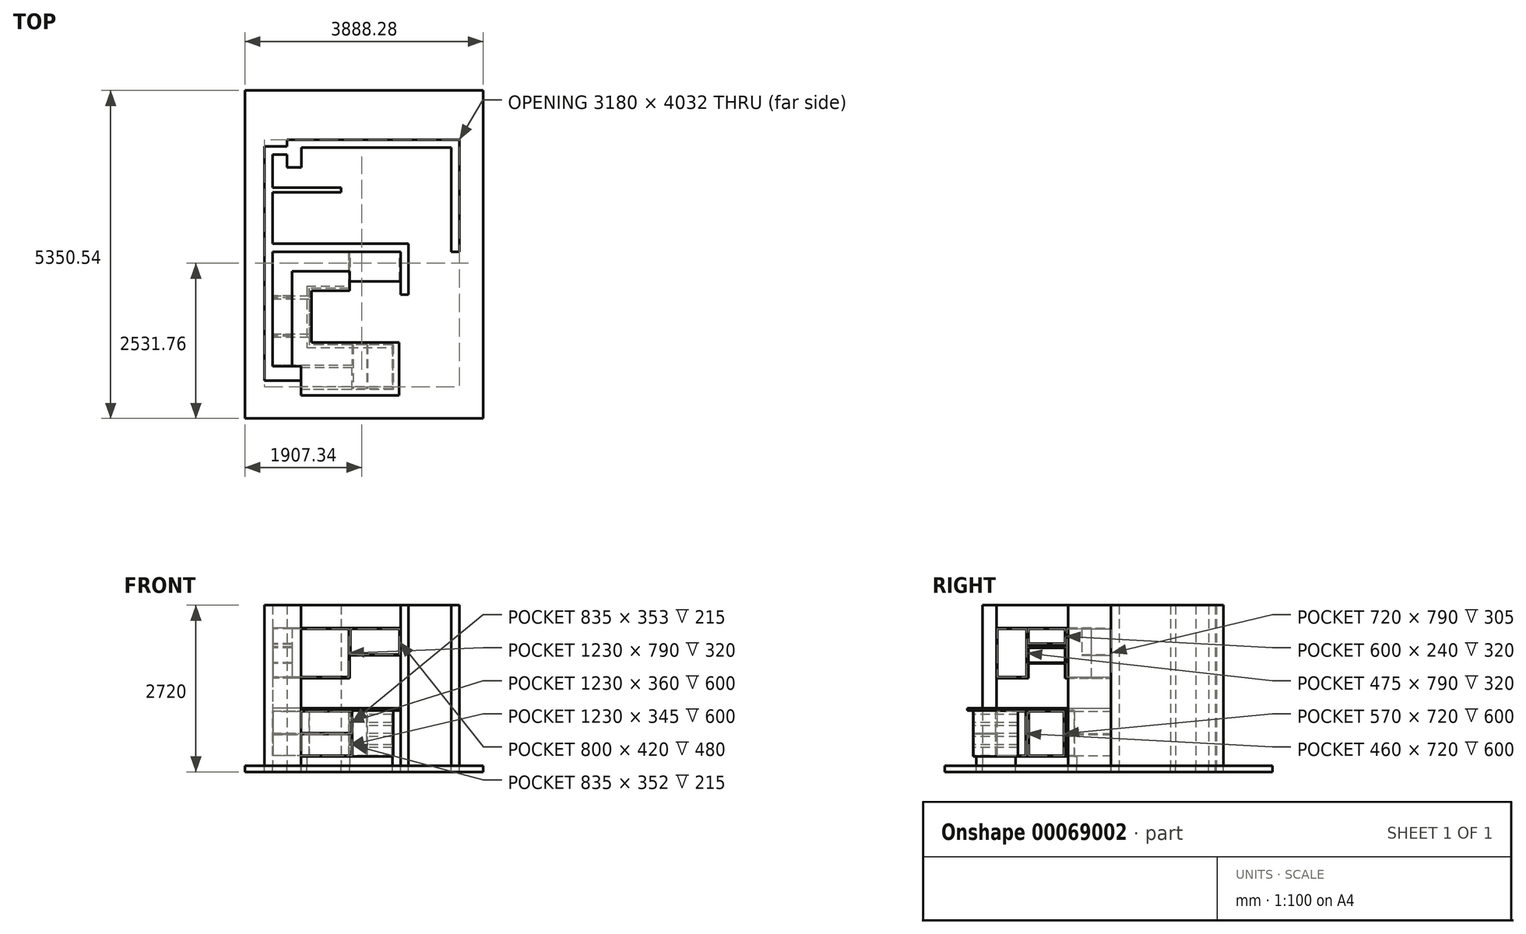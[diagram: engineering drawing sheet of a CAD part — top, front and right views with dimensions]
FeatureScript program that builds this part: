
annotation { "Feature Type Name" : "Feature", "Feature Type Description" : "" }
export const myFeature = defineFeature(function(context is Context, id is Id, definition is map)
    precondition{}
    {
        {
            var Q0;
            Q0=qCreatedBy(makeId("Top.planeOp"),FACE);
            var sketch = newSketch(context, id + "F0", { "sketchPlane" : qUnion([Q0])});
            skLineSegment(sketch, "E0.bottom", {"start": v(-1600, 1700) * mm, "end": v(-1830, 1700) * mm});
            skLineSegment(sketch, "E0.top", {"start": v(-1600, 1250) * mm, "end": v(-1830, 1250) * mm});
            skLineSegment(sketch, "E0.right", {"start": v(-1830, 1700) * mm, "end": v(-1830, 1250) * mm});
            skLineSegment(sketch, "E1", {"start": v(-1830, 1460) * mm, "end": v(-2070, 1460) * mm});
            skLineSegment(sketch, "E2", {"start": v(-1600, 1250) * mm, "end": v(-1600, 1700) * mm});
            skLineSegment(sketch, "E3", {"start": v(-2070, 1460) * mm, "end": v(-2070, -2000) * mm});
            skLineSegment(sketch, "E4.0", {"start": v(-2200, 1590) * mm, "end": v(-2200, -2000) * mm});
            skLineSegment(sketch, "E4.1", {"start": v(-1830, 1590) * mm, "end": v(-2200, 1590) * mm});
            skLineSegment(sketch, "E5.bottom", {"start": v(-2200, -2000) * mm, "end": v(-1605, -2000) * mm});
            skLineSegment(sketch, "E5.top", {"start": v(-2200, -2230) * mm, "end": v(-1605, -2230) * mm});
            skLineSegment(sketch, "E5.left", {"start": v(-2200, -2000) * mm, "end": v(-2200, -2230) * mm});
            skLineSegment(sketch, "E5.right", {"start": v(-1605, -2000) * mm, "end": v(-1605, -2230) * mm});
            skLineSegment(sketch, "E6", {"start": v(980, 1700) * mm, "end": v(980, -132.1) * mm});
            skLineSegment(sketch, "E7", {"start": v(980, -132.1) * mm, "end": v(850, -130) * mm});
            skLineSegment(sketch, "E8", {"start": v(850, 1570) * mm, "end": v(-1600, 1570) * mm});
            skLineSegment(sketch, "E9", {"start": v(980, 1700) * mm, "end": v(-1600, 1700) * mm});
            skLineSegment(sketch, "E10", {"start": v(850, 1570) * mm, "end": v(850, -130) * mm});
            skLineSegment(sketch, "E11", {"start": v(150, 0) * mm, "end": v(-2070, 0) * mm});
            skLineSegment(sketch, "E12.top", {"start": v(150, -830) * mm, "end": v(20, -830) * mm});
            skLineSegment(sketch, "E12.right", {"start": v(20, -130) * mm, "end": v(20, -830) * mm});
            skLineSegment(sketch, "E13", {"start": v(20, -130) * mm, "end": v(-2070, -130) * mm});
            skLineSegment(sketch, "E14", {"start": v(150, 0) * mm, "end": v(150, -830) * mm});
            skLineSegment(sketch, "E15", {"start": v(-1510, -690) * mm, "end": v(-1510, -1690) * mm});
            skLineSegment(sketch, "E16", {"start": v(-1510, -1690) * mm, "end": v(-110, -1690) * mm});
            skLineSegment(sketch, "E17", {"start": v(-1510, -690) * mm, "end": v(-810, -690) * mm});
            skLineSegment(sketch, "E18", {"start": v(-810, -690) * mm, "end": v(-810, -130) * mm});
            skLineSegment(sketch, "E19", {"start": v(-110, -1690) * mm, "end": v(-110, -2332) * mm});
            skLineSegment(sketch, "E20", {"start": v(-110, -2332) * mm, "end": v(-1605, -2332) * mm});
            skLineSegment(sketch, "E21", {"start": v(-1605, -2332) * mm, "end": v(-1605, -2230) * mm});
            skLineSegment(sketch, "E22", {"start": v(-2070, 920) * mm, "end": v(-950, 920) * mm});
            skLineSegment(sketch, "E23", {"start": v(-950, 920) * mm, "end": v(-950, 840) * mm});
            skLineSegment(sketch, "E24", {"start": v(-950, 840) * mm, "end": v(-2070, 840) * mm});
            skSolve(sketch);
        }
        {
            var Q0;
            {var subQ0=sQuery(id+"F0.wireOp",EDGE,"E11");Q0=makeQuery(id+"F0.imprint","IMPRINT",FACE,{"disambiguationData":[TD([[makeQuery(id+"F0.imprint","IMPRINT",EDGE,{"derivedFrom":subQ0}),1.0]])]});}
            var Q1;
            {var subQ3=sQuery(id+"F0.wireOp",EDGE,"E1");Q1=makeQuery(id+"F0.imprint","IMPRINT",FACE,{"disambiguationData":[TD([[makeQuery(id+"F0.imprint","IMPRINT",EDGE,{"derivedFrom":subQ3}),-1.0]])]});}
            var Q2;
            Q2=makeQuery(id+"F0.imprint","IMPRINT",FACE,{"disambiguationData":[TD([[makeQuery(id+"F0.imprint","IMPRINT",EDGE,{"derivedFrom":sQuery(id+"F0.wireOp",EDGE,"E6")}),-1.0]])]});
            var Q3;
            {var subQ3=sQuery(id+"F0.wireOp",EDGE,"E0.bottom");Q3=makeQuery(id+"F0.imprint","IMPRINT",FACE,{"disambiguationData":[TD([[makeQuery(id+"F0.imprint","IMPRINT",EDGE,{"derivedFrom":subQ3}),1.0]])]});}
            var Q4;
            Q4=makeQuery(id+"F0.imprint","IMPRINT",FACE,{"disambiguationData":[TD([[makeQuery(id+"F0.imprint","IMPRINT",EDGE,{"derivedFrom":sQuery(id+"F0.wireOp",EDGE,"E5.top")}),1.0]])]});
            var Q5;
            {var subQ0=sQuery(id+"F0.wireOp",EDGE,"E22");Q5=makeQuery(id+"F0.imprint","IMPRINT",FACE,{"disambiguationData":[TD([[makeQuery(id+"F0.imprint","IMPRINT",EDGE,{"derivedFrom":subQ0}),-1.0]])]});}
            extrude(context, id + "F1", {"entities" : qUnion([Q0, Q1, Q2, Q3, Q4, Q5]), "depth" : 2620 * mm});
        }
        {
            var Q0;
            Q0=makeQuery(id+"F1.opExtrude","SWEPT_FACE",FACE,{"disambiguationData":[OSD([sQuery(id+"F0.wireOp",EDGE,"E13")])]});
            var sketch = newSketch(context, id + "F2", { "sketchPlane" : qUnion([Q0])});
            skLineSegment(sketch, "E25.bottom", {"start": v(-810, 1430) * mm, "end": v(-2070, 1430) * mm});
            skLineSegment(sketch, "E25.top", {"start": v(-810, 2250) * mm, "end": v(-2070, 2250) * mm});
            skLineSegment(sketch, "E25.left", {"start": v(-810, 1430) * mm, "end": v(-810, 2250) * mm});
            skLineSegment(sketch, "E25.right", {"start": v(-2070, 1430) * mm, "end": v(-2070, 2250) * mm});
            skLineSegment(sketch, "E26.0", {"start": v(-825, 2235) * mm, "end": v(-2055, 2235) * mm});
            skLineSegment(sketch, "E26.1", {"start": v(-825, 1445) * mm, "end": v(-825, 2235) * mm});
            skLineSegment(sketch, "E26.2", {"start": v(-825, 1445) * mm, "end": v(-2055, 1445) * mm});
            skLineSegment(sketch, "E26.3", {"start": v(-2055, 1445) * mm, "end": v(-2055, 2235) * mm});
            skSolve(sketch);
        }
        {
            var Q0;
            Q0=makeQuery(id+"F2.imprint","IMPRINT",FACE,{"disambiguationData":[TD([[makeQuery(id+"F2.imprint","IMPRINT",EDGE,{"derivedFrom":sQuery(id+"F2.wireOp",EDGE,"E25.bottom")}),-1.0]])]});
            extrude(context, id + "F3", {"entities" : qUnion([Q0]), "operationType" : NewBodyOperationType.ADD, "depth" : 320 * mm});
        }
        {
            var Q0;
            {var subQ0=sQuery(id+"F0.wireOp",EDGE,"E3");Q0=makeQuery(id+"F1.opExtrude","SWEPT_FACE",FACE,{"disambiguationData":[OSD([subQ0]),TDD([makeQuery(id+"F0.imprint","IMPRINT",EDGE,{"disambiguationData":[TD([[makeQuery(id+"F0.imprint","INTERSECT",VERTEX,{"derivedFrom":[subQ0,sQuery(id+"F0.wireOp",EDGE,"E5.bottom")]}),1.0]])],"derivedFrom":subQ0})])]});}
            var sketch = newSketch(context, id + "F4", { "sketchPlane" : qUnion([Q0])});
            skLineSegment(sketch, "E27.bottom", {"start": v(-450, 2250) * mm, "end": v(-865, 2250) * mm});
            skLineSegment(sketch, "E27.top", {"start": v(-450, 1430) * mm, "end": v(-865, 1430) * mm});
            skLineSegment(sketch, "E27.right", {"start": v(-865, 2250) * mm, "end": v(-865, 1430) * mm});
            skLineSegment(sketch, "E28.0", {"start": v(-850, 2235) * mm, "end": v(-850, 1445) * mm});
            skLineSegment(sketch, "E29", {"start": v(-645, 1445) * mm, "end": v(-645, 2235) * mm});
            skLineSegment(sketch, "E30.0", {"start": v(-630, 1445) * mm, "end": v(-630, 2235) * mm});
            skLineSegment(sketch, "E31", {"start": v(-450, 2250) * mm, "end": v(-450, 2235) * mm});
            skLineSegment(sketch, "E32", {"start": v(-850, 2235) * mm, "end": v(-450, 2235) * mm});
            skLineSegment(sketch, "E33", {"start": v(-450, 1430) * mm, "end": v(-450, 1445) * mm});
            skLineSegment(sketch, "E34", {"start": v(-850, 1445) * mm, "end": v(-450, 1445) * mm});
            skSolve(sketch);
        }
        {
            var Q0;
            Q0=makeQuery(id+"F4.imprint","IMPRINT",FACE,{"disambiguationData":[TD([[makeQuery(id+"F4.imprint","IMPRINT",EDGE,{"derivedFrom":sQuery(id+"F4.wireOp",EDGE,"E27.bottom")}),1.0]])]});
            extrude(context, id + "F5", {"entities" : qUnion([Q0]), "operationType" : NewBodyOperationType.ADD, "depth" : 320 * mm});
        }
        {
            var Q0;
            {var subQ1=sQuery(id+"F2.wireOp",EDGE,"E26.0");var subQ2=sQuery(id+"F0.wireOp",EDGE,"E3");Q0=makeQuery(id+"F5.boolean.opBoolean","SPLIT",FACE,{"disambiguationData":[TD([makeQuery(id+"F3.opExtrude","SWEPT_FACE",FACE,{"disambiguationData":[OSD([subQ1])]})])],"derivedFrom":makeQuery(id+"F1.opExtrude","SWEPT_FACE",FACE,{"disambiguationData":[OSD([subQ2]),TDD([makeQuery(id+"F0.imprint","IMPRINT",EDGE,{"disambiguationData":[TD([[makeQuery(id+"F0.imprint","INTERSECT",VERTEX,{"derivedFrom":[subQ2,sQuery(id+"F0.wireOp",EDGE,"E5.bottom")]}),1.0]])],"derivedFrom":subQ2})])]})});}
            extrude(context, id + "F6", {"entities" : qUnion([Q0]), "operationType" : NewBodyOperationType.ADD, "depth" : 15 * mm});
        }
        {
            var Q0;
            {var subQ2=sQuery(id+"F0.wireOp",EDGE,"E5.bottom");var subQ3=sQuery(id+"F0.wireOp",EDGE,"E3");Q0=makeQuery(id+"F5.boolean.opBoolean","SPLIT",FACE,{"disambiguationData":[TD([makeQuery(id+"F1.opExtrude","SWEPT_FACE",FACE,{"disambiguationData":[OSD([subQ2])]})])],"derivedFrom":makeQuery(id+"F1.opExtrude","SWEPT_FACE",FACE,{"disambiguationData":[OSD([subQ3]),TDD([makeQuery(id+"F0.imprint","IMPRINT",EDGE,{"disambiguationData":[TD([[makeQuery(id+"F0.imprint","INTERSECT",VERTEX,{"derivedFrom":[subQ3,subQ2]}),1.0]])],"derivedFrom":subQ3})])]})});}
            var sketch = newSketch(context, id + "F7", { "sketchPlane" : qUnion([Q0])});
            skLineSegment(sketch, "E35.bottom", {"start": v(-865, 2250) * mm, "end": v(-1495, 2250) * mm});
            skLineSegment(sketch, "E35.left", {"start": v(-865, 2250) * mm, "end": v(-865, 1430) * mm});
            skLineSegment(sketch, "E35.right", {"start": v(-1495, 2250) * mm, "end": v(-1495, 1430) * mm});
            skLineSegment(sketch, "E36.0", {"start": v(-880, 2235) * mm, "end": v(-880, 1430) * mm});
            skLineSegment(sketch, "E36.1", {"start": v(-880, 2235) * mm, "end": v(-1480, 2235) * mm});
            skLineSegment(sketch, "E36.2", {"start": v(-1480, 2235) * mm, "end": v(-1480, 1430) * mm});
            skLineSegment(sketch, "E37", {"start": v(-1480, 1670) * mm, "end": v(-880, 1670) * mm});
            skLineSegment(sketch, "E38", {"start": v(-1480, 1430) * mm, "end": v(-1495, 1430) * mm});
            skLineSegment(sketch, "E39", {"start": v(-865, 1430) * mm, "end": v(-880, 1430) * mm});
            skLineSegment(sketch, "E40.0", {"start": v(-1480, 1685) * mm, "end": v(-880, 1685) * mm});
            skLineSegment(sketch, "E41", {"start": v(-1480, 1925) * mm, "end": v(-880, 1925) * mm});
            skLineSegment(sketch, "E42", {"start": v(-1480, 1995) * mm, "end": v(-880, 1995) * mm});
            skLineSegment(sketch, "E43.0", {"start": v(-1480, 1980) * mm, "end": v(-880, 1980) * mm});
            skLineSegment(sketch, "E44.0", {"start": v(-1480, 1940) * mm, "end": v(-880, 1940) * mm});
            skSolve(sketch);
        }
        {
            var Q0;
            Q0=makeQuery(id+"F7.imprint","IMPRINT",FACE,{"disambiguationData":[TD([[makeQuery(id+"F7.imprint","IMPRINT",EDGE,{"derivedFrom":sQuery(id+"F7.wireOp",EDGE,"E35.bottom")}),1.0]])]});
            var Q1;
            {var subQ0=sQuery(id+"F7.wireOp",EDGE,"E42");Q1=makeQuery(id+"F7.imprint","IMPRINT",FACE,{"disambiguationData":[TD([[makeQuery(id+"F7.imprint","IMPRINT",EDGE,{"derivedFrom":subQ0}),-1.0]])]});}
            var Q2;
            {var subQ0=sQuery(id+"F7.wireOp",EDGE,"E41");Q2=makeQuery(id+"F7.imprint","IMPRINT",FACE,{"disambiguationData":[TD([[makeQuery(id+"F7.imprint","IMPRINT",EDGE,{"derivedFrom":subQ0}),1.0]])]});}
            var Q3;
            {var subQ0=sQuery(id+"F7.wireOp",EDGE,"E37");Q3=makeQuery(id+"F7.imprint","IMPRINT",FACE,{"disambiguationData":[TD([[makeQuery(id+"F7.imprint","IMPRINT",EDGE,{"derivedFrom":subQ0}),1.0]])]});}
            extrude(context, id + "F8", {"entities" : qUnion([Q0, Q1, Q2, Q3]), "operationType" : NewBodyOperationType.ADD, "depth" : 320 * mm});
        }
        {
            var Q0;
            {var subQ7=sQuery(id+"F0.wireOp",EDGE,"E5.bottom");var subQ8=sQuery(id+"F0.wireOp",EDGE,"E3");var subQ11=makeQuery(id+"F1.opExtrude","SWEPT_FACE",FACE,{"disambiguationData":[OSD([subQ7])]});Q0=makeQuery(id+"F8.boolean.opBoolean","SPLIT",FACE,{"disambiguationData":[TD([subQ11])],"derivedFrom":makeQuery(id+"F5.boolean.opBoolean","SPLIT",FACE,{"disambiguationData":[TD([subQ11])],"derivedFrom":makeQuery(id+"F1.opExtrude","SWEPT_FACE",FACE,{"disambiguationData":[OSD([subQ8]),TDD([makeQuery(id+"F0.imprint","IMPRINT",EDGE,{"disambiguationData":[TD([[makeQuery(id+"F0.imprint","INTERSECT",VERTEX,{"derivedFrom":[subQ8,subQ7]}),1.0]])],"derivedFrom":subQ8})])]})})});}
            var sketch = newSketch(context, id + "F9", { "sketchPlane" : qUnion([Q0])});
            skLineSegment(sketch, "E45.bottom", {"start": v(-1495, 2250) * mm, "end": v(-2000, 2250) * mm});
            skLineSegment(sketch, "E45.top", {"start": v(-1495, 1430) * mm, "end": v(-2000, 1430) * mm});
            skLineSegment(sketch, "E45.left", {"start": v(-1495, 2250) * mm, "end": v(-1495, 1430) * mm});
            skLineSegment(sketch, "E45.right", {"start": v(-2000, 2250) * mm, "end": v(-2000, 1430) * mm});
            skLineSegment(sketch, "E46.0", {"start": v(-1510, 2235) * mm, "end": v(-1985, 2235) * mm});
            skLineSegment(sketch, "E46.1", {"start": v(-1510, 2235) * mm, "end": v(-1510, 1445) * mm});
            skLineSegment(sketch, "E46.2", {"start": v(-1510, 1445) * mm, "end": v(-1985, 1445) * mm});
            skLineSegment(sketch, "E46.3", {"start": v(-1985, 2235) * mm, "end": v(-1985, 1445) * mm});
            skSolve(sketch);
        }
        {
            var Q0;
            Q0=makeQuery(id+"F9.imprint","IMPRINT",FACE,{"disambiguationData":[TD([[makeQuery(id+"F9.imprint","IMPRINT",EDGE,{"derivedFrom":sQuery(id+"F9.wireOp",EDGE,"E45.bottom")}),1.0]])]});
            extrude(context, id + "F10", {"entities" : qUnion([Q0]), "operationType" : NewBodyOperationType.ADD, "depth" : 320 * mm});
        }
        {
            var Q0;
            {var subQ6=sQuery(id+"F0.wireOp",EDGE,"E5.right");Q0=makeQuery(id+"F0.imprint","IMPRINT",FACE,{"disambiguationData":[TD([[makeQuery(id+"F0.imprint","IMPRINT",EDGE,{"derivedFrom":subQ6}),1.0]])]});}
            extrude(context, id + "F11", {"entities" : qUnion([Q0]), "operationType" : NewBodyOperationType.ADD, "depth" : 150 * mm});
        }
        {
            var Q0;
            {var subQ0=sQuery(id+"F0.wireOp",EDGE,"E12.right");var subQ3=sQuery(id+"F0.wireOp",EDGE,"E13");Q0=makeQuery(id+"F3.boolean.opBoolean","SPLIT",FACE,{"disambiguationData":[TD([makeQuery(id+"F1.opExtrude","SWEPT_FACE",FACE,{"disambiguationData":[OSD([subQ0])]})])],"derivedFrom":makeQuery(id+"F1.opExtrude","SWEPT_FACE",FACE,{"disambiguationData":[OSD([subQ3])]})});}
            var sketch = newSketch(context, id + "F12", { "sketchPlane" : qUnion([Q0])});
            skLineSegment(sketch, "E47.bottom", {"start": v(-810, 150) * mm, "end": v(-2070, 150) * mm});
            skLineSegment(sketch, "E47.top", {"start": v(-810, 900) * mm, "end": v(-2070, 900) * mm});
            skLineSegment(sketch, "E47.left", {"start": v(-810, 150) * mm, "end": v(-810, 900) * mm});
            skLineSegment(sketch, "E47.right", {"start": v(-2070, 150) * mm, "end": v(-2070, 900) * mm});
            skLineSegment(sketch, "E48.0", {"start": v(-825, 165) * mm, "end": v(-825, 885) * mm});
            skLineSegment(sketch, "E48.1", {"start": v(-825, 165) * mm, "end": v(-2055, 165) * mm});
            skLineSegment(sketch, "E48.2", {"start": v(-2055, 165) * mm, "end": v(-2055, 885) * mm});
            skLineSegment(sketch, "E48.3", {"start": v(-825, 885) * mm, "end": v(-2055, 885) * mm});
            skPoint(sketch, "E49.oppositeSnap0", {"position": v(-2055, 525) * mm});
            skLineSegment(sketch, "E49.bottom", {"start": v(-2055, 510) * mm, "end": v(-1604.18, 510) * mm});
            skLineSegment(sketch, "E49.top", {"start": v(-2055, 525) * mm, "end": v(-1604.18, 525) * mm});
            skLineSegment(sketch, "E49.left", {"start": v(-2055, 510) * mm, "end": v(-2055, 525) * mm});
            skLineSegment(sketch, "E49.right", {"start": v(-1604.18, 510) * mm, "end": v(-1604.18, 525) * mm});
            skLineSegment(sketch, "E50.bottom", {"start": v(-1604.18, 510) * mm, "end": v(-825, 510) * mm});
            skLineSegment(sketch, "E50.top", {"start": v(-1604.18, 525) * mm, "end": v(-825, 525) * mm});
            skLineSegment(sketch, "E50.right", {"start": v(-825, 510) * mm, "end": v(-825, 525) * mm});
            skSolve(sketch);
        }
        {
            var Q0;
            Q0=makeQuery(id+"F12.imprint","IMPRINT",FACE,{"disambiguationData":[TD([[makeQuery(id+"F12.imprint","IMPRINT",EDGE,{"derivedFrom":sQuery(id+"F12.wireOp",EDGE,"E47.bottom")}),-1.0]])]});
            var Q1;
            Q1=makeQuery(id+"F12.imprint","IMPRINT",FACE,{"disambiguationData":[TD([[makeQuery(id+"F12.imprint","IMPRINT",EDGE,{"derivedFrom":sQuery(id+"F12.wireOp",EDGE,"E50.bottom")}),1.0]])]});
            var Q2;
            Q2=makeQuery(id+"F12.imprint","IMPRINT",FACE,{"disambiguationData":[TD([[makeQuery(id+"F12.imprint","IMPRINT",EDGE,{"derivedFrom":sQuery(id+"F12.wireOp",EDGE,"E49.bottom")}),1.0]])]});
            extrude(context, id + "F13", {"entities" : qUnion([Q0, Q1, Q2]), "operationType" : NewBodyOperationType.ADD, "depth" : 600 * mm});
        }
        {
            var Q0;
            {var subQ23=sQuery(id+"F0.wireOp",EDGE,"E5.bottom");var subQ26=sQuery(id+"F0.wireOp",EDGE,"E3");var subQ33=makeQuery(id+"F3.opExtrude","SWEPT_FACE",FACE,{"disambiguationData":[OSD([sQuery(id+"F2.wireOp",EDGE,"E25.bottom")])]});var subQ35=makeQuery(id+"F1.opExtrude","SWEPT_FACE",FACE,{"disambiguationData":[OSD([subQ23])]});Q0=makeQuery(id+"F10.boolean.opBoolean","SPLIT",FACE,{"disambiguationData":[TD([subQ33])],"derivedFrom":makeQuery(id+"F8.boolean.opBoolean","SPLIT",FACE,{"disambiguationData":[TD([subQ35])],"derivedFrom":makeQuery(id+"F5.boolean.opBoolean","SPLIT",FACE,{"disambiguationData":[TD([subQ35])],"derivedFrom":makeQuery(id+"F1.opExtrude","SWEPT_FACE",FACE,{"disambiguationData":[OSD([subQ26]),TDD([makeQuery(id+"F0.imprint","IMPRINT",EDGE,{"disambiguationData":[TD([[makeQuery(id+"F0.imprint","INTERSECT",VERTEX,{"derivedFrom":[subQ26,subQ23]}),1.0]])],"derivedFrom":subQ26})])]})})})});}
            var sketch = newSketch(context, id + "F14", { "sketchPlane" : qUnion([Q0])});
            skLineSegment(sketch, "E51", {"start": v(-1525, 165) * mm, "end": v(-1525, 885) * mm});
            skLineSegment(sketch, "E52", {"start": v(-855, 885) * mm, "end": v(-855, 165) * mm});
            skLineSegment(sketch, "E53.0", {"start": v(-1475, 165) * mm, "end": v(-1475, 885) * mm});
            skLineSegment(sketch, "E54.0", {"start": v(-905, 885) * mm, "end": v(-905, 165) * mm});
            skLineSegment(sketch, "E55", {"start": v(-730, 900) * mm, "end": v(-730, 885) * mm});
            skLineSegment(sketch, "E56", {"start": v(-730, 150) * mm, "end": v(-730, 165) * mm});
            skLineSegment(sketch, "E57", {"start": v(-855, 510) * mm, "end": v(-730, 510) * mm});
            skLineSegment(sketch, "E58.0", {"start": v(-855, 525) * mm, "end": v(-730, 525) * mm});
            skLineSegment(sketch, "E59", {"start": v(-730, 525) * mm, "end": v(-730, 510) * mm});
            skLineSegment(sketch, "E60", {"start": v(-730, 900) * mm, "end": v(-2000, 900) * mm});
            skLineSegment(sketch, "E61", {"start": v(-2000, 900) * mm, "end": v(-2000, 150) * mm});
            skLineSegment(sketch, "E62", {"start": v(-2000, 150) * mm, "end": v(-730, 150) * mm});
            skLineSegment(sketch, "E63", {"start": v(-730, 165) * mm, "end": v(-1985, 165) * mm});
            skLineSegment(sketch, "E64", {"start": v(-1985, 165) * mm, "end": v(-1985, 885) * mm});
            skLineSegment(sketch, "E65", {"start": v(-1985, 885) * mm, "end": v(-730, 885) * mm});
            skSolve(sketch);
        }
        {
            var Q0;
            {var subQ0=sQuery(id+"F14.wireOp",EDGE,"E51");Q0=makeQuery(id+"F14.imprint","IMPRINT",FACE,{"disambiguationData":[TD([[makeQuery(id+"F14.imprint","IMPRINT",EDGE,{"derivedFrom":subQ0}),-1.0]])]});}
            var Q1;
            Q1=makeQuery(id+"F14.imprint","IMPRINT",FACE,{"disambiguationData":[TD([[makeQuery(id+"F14.imprint","IMPRINT",EDGE,{"derivedFrom":sQuery(id+"F14.wireOp",EDGE,"178934f9-c5af-4424-81ba-d585937f0cbb.bottom")}),-1.0]])]});
            var Q2;
            {var subQ0=sQuery(id+"F14.wireOp",EDGE,"E52");Q2=makeQuery(id+"F14.imprint","IMPRINT",FACE,{"disambiguationData":[TD([[makeQuery(id+"F14.imprint","IMPRINT",EDGE,{"derivedFrom":subQ0}),-1.0]])]});}
            var Q3;
            {var subQ0=sQuery(id+"F14.wireOp",EDGE,"E57");Q3=makeQuery(id+"F14.imprint","IMPRINT",FACE,{"disambiguationData":[TD([[makeQuery(id+"F14.imprint","IMPRINT",EDGE,{"derivedFrom":subQ0}),1.0]])]});}
            var Q4;
            {var subQ10=sQuery(id+"F14.wireOp",EDGE,"E55");Q4=makeQuery(id+"F14.imprint","IMPRINT",FACE,{"disambiguationData":[TD([[makeQuery(id+"F14.imprint","IMPRINT",EDGE,{"derivedFrom":subQ10}),-1.0]])]});}
            extrude(context, id + "F15", {"entities" : qUnion([Q0, Q1, Q2, Q3, Q4]), "operationType" : NewBodyOperationType.ADD, "depth" : 600 * mm});
        }
        {
            var Q0;
            {var subQ0=sQuery(id+"F0.wireOp",EDGE,"E12.right");var subQ1=makeQuery(id+"F1.opExtrude","SWEPT_FACE",FACE,{"disambiguationData":[OSD([subQ0])]});var subQ4=sQuery(id+"F0.wireOp",EDGE,"E13");Q0=makeQuery(id+"F13.boolean.opBoolean","SPLIT",FACE,{"disambiguationData":[TD([subQ1])],"derivedFrom":makeQuery(id+"F3.boolean.opBoolean","SPLIT",FACE,{"disambiguationData":[TD([subQ1])],"derivedFrom":makeQuery(id+"F1.opExtrude","SWEPT_FACE",FACE,{"disambiguationData":[OSD([subQ4])]})})});}
            var sketch = newSketch(context, id + "F16", { "sketchPlane" : qUnion([Q0])});
            skLineSegment(sketch, "E66.bottom", {"start": v(-810, 2250) * mm, "end": v(20, 2250) * mm});
            skLineSegment(sketch, "E66.top", {"start": v(-810, 1800) * mm, "end": v(20, 1800) * mm});
            skLineSegment(sketch, "E66.left", {"start": v(-810, 2250) * mm, "end": v(-810, 1800) * mm});
            skLineSegment(sketch, "E66.right", {"start": v(20, 2250) * mm, "end": v(20, 1800) * mm});
            skLineSegment(sketch, "E67.0", {"start": v(-795, 1815) * mm, "end": v(5, 1815) * mm});
            skLineSegment(sketch, "E67.1", {"start": v(-795, 2235) * mm, "end": v(-795, 1815) * mm});
            skLineSegment(sketch, "E67.2", {"start": v(-795, 2235) * mm, "end": v(5, 2235) * mm});
            skLineSegment(sketch, "E67.3", {"start": v(5, 2235) * mm, "end": v(5, 1815) * mm});
            skSolve(sketch);
        }
        {
            var Q0;
            Q0=makeQuery(id+"F16.imprint","IMPRINT",FACE,{"disambiguationData":[TD([[makeQuery(id+"F16.imprint","IMPRINT",EDGE,{"derivedFrom":sQuery(id+"F16.wireOp",EDGE,"E66.bottom")}),-1.0]])]});
            extrude(context, id + "F17", {"entities" : qUnion([Q0]), "operationType" : NewBodyOperationType.ADD, "depth" : 480 * mm});
        }
        {
            var Q0;
            {var subQ0=sQuery(id+"F0.wireOp",EDGE,"E13");var subQ1=sQuery(id+"F0.wireOp",EDGE,"E5.right");var subQ2=sQuery(id+"F0.wireOp",EDGE,"E5.bottom");var subQ3=sQuery(id+"F0.wireOp",EDGE,"E3");Q0=makeQuery(id+"F11.boolean.opBoolean","MERGE",FACE,{"derivedFrom":[makeQuery(id+"F1.opExtrude","CAP_FACE",FACE,{"disambiguationData":[OSD([sQuery(id+"F0.wireOp",EDGE,"E0.bottom"),sQuery(id+"F0.wireOp",EDGE,"E0.top"),sQuery(id+"F0.wireOp",EDGE,"E0.right"),sQuery(id+"F0.wireOp",EDGE,"E1"),sQuery(id+"F0.wireOp",EDGE,"E2"),subQ3,sQuery(id+"F0.wireOp",EDGE,"E4.0"),sQuery(id+"F0.wireOp",EDGE,"E4.1"),subQ2,sQuery(id+"F0.wireOp",EDGE,"E5.top"),sQuery(id+"F0.wireOp",EDGE,"E5.left"),subQ1,sQuery(id+"F0.wireOp",EDGE,"E6"),sQuery(id+"F0.wireOp",EDGE,"E7"),sQuery(id+"F0.wireOp",EDGE,"E8"),sQuery(id+"F0.wireOp",EDGE,"E9"),sQuery(id+"F0.wireOp",EDGE,"E10"),sQuery(id+"F0.wireOp",EDGE,"E11"),sQuery(id+"F0.wireOp",EDGE,"E12.top"),sQuery(id+"F0.wireOp",EDGE,"E12.right"),subQ0,sQuery(id+"F0.wireOp",EDGE,"E14")])],"isStart":true}),makeQuery(id+"F11.opExtrude","CAP_FACE",FACE,{"disambiguationData":[OSD([subQ3,subQ2,subQ1,subQ0,sQuery(id+"F0.wireOp",EDGE,"E15"),sQuery(id+"F0.wireOp",EDGE,"E16"),sQuery(id+"F0.wireOp",EDGE,"E17"),sQuery(id+"F0.wireOp",EDGE,"E18"),sQuery(id+"F0.wireOp",EDGE,"E19"),sQuery(id+"F0.wireOp",EDGE,"E20"),sQuery(id+"F0.wireOp",EDGE,"E21")])],"isStart":true})]});}
            var sketch = newSketch(context, id + "F18", { "sketchPlane" : qUnion([Q0])});
            skLineSegment(sketch, "E68.bottom", {"start": v(-2517.34, 2847.76) * mm, "end": v(1370.94, 2847.76) * mm});
            skLineSegment(sketch, "E68.top", {"start": v(-2517.34, -2502.78) * mm, "end": v(1370.94, -2502.78) * mm});
            skLineSegment(sketch, "E68.left", {"start": v(-2517.34, 2847.76) * mm, "end": v(-2517.34, -2502.78) * mm});
            skLineSegment(sketch, "E68.right", {"start": v(1370.94, 2847.76) * mm, "end": v(1370.94, -2502.78) * mm});
            skSolve(sketch);
        }
        {
            var Q0;
            Q0=makeQuery(id+"F18.imprint","IMPRINT",FACE,{"disambiguationData":[TD([[makeQuery(id+"F18.imprint","IMPRINT",EDGE,{"derivedFrom":sQuery(id+"F18.wireOp",EDGE,"E68.bottom")}),-1.0]])]});
            extrude(context, id + "F19", {"entities" : qUnion([Q0]), "depth" : 100 * mm});
        }
        {
            var Q0;
            Q0=makeQuery(id+"F15.opExtrude","CAP_FACE",FACE,{"disambiguationData":[OSD([sQuery(id+"F14.wireOp",EDGE,"E51"),sQuery(id+"F14.wireOp",EDGE,"E52"),sQuery(id+"F14.wireOp",EDGE,"E53.0"),sQuery(id+"F14.wireOp",EDGE,"E54.0"),sQuery(id+"F14.wireOp",EDGE,"E55"),sQuery(id+"F14.wireOp",EDGE,"E56"),sQuery(id+"F14.wireOp",EDGE,"E57"),sQuery(id+"F14.wireOp",EDGE,"E58.0"),sQuery(id+"F14.wireOp",EDGE,"E59"),sQuery(id+"F14.wireOp",EDGE,"E60"),sQuery(id+"F14.wireOp",EDGE,"E61"),sQuery(id+"F14.wireOp",EDGE,"E62"),sQuery(id+"F14.wireOp",EDGE,"E63"),sQuery(id+"F14.wireOp",EDGE,"E64"),sQuery(id+"F14.wireOp",EDGE,"E65")])],"isStart":false});
            var sketch = newSketch(context, id + "F20", { "sketchPlane" : qUnion([Q0])});
            skLineSegment(sketch, "E69", {"start": v(-1650, 150) * mm, "end": v(-2000, 150) * mm});
            skLineSegment(sketch, "E70", {"start": v(-2000, 150) * mm, "end": v(-2000, 900) * mm});
            skLineSegment(sketch, "E71", {"start": v(-2000, 900) * mm, "end": v(-1650, 900) * mm});
            skLineSegment(sketch, "E72", {"start": v(-1650, 150) * mm, "end": v(-1650, 165) * mm});
            skLineSegment(sketch, "E73", {"start": v(-1650, 165) * mm, "end": v(-1985, 165) * mm});
            skLineSegment(sketch, "E74", {"start": v(-1985, 165) * mm, "end": v(-1985, 885) * mm});
            skLineSegment(sketch, "E75", {"start": v(-1985, 885) * mm, "end": v(-1650, 885) * mm});
            skLineSegment(sketch, "E76", {"start": v(-1650, 885) * mm, "end": v(-1650, 900) * mm});
            skSolve(sketch);
        }
        {
            var Q0;
            {var subQ0=sQuery(id+"F20.wireOp",EDGE,"E70");Q0=makeQuery(id+"F20.imprint","IMPRINT",FACE,{"disambiguationData":[TD([[makeQuery(id+"F20.imprint","IMPRINT",EDGE,{"derivedFrom":subQ0}),1.0]])]});}
            extrude(context, id + "F21", {"entities" : qUnion([Q0]), "operationType" : NewBodyOperationType.ADD, "depth" : 700 * mm});
        }
        {
            var Q0;
            Q0=makeQuery(id+"F1.opExtrude","SWEPT_FACE",FACE,{"disambiguationData":[OSD([sQuery(id+"F0.wireOp",EDGE,"E5.right")])]});
            var sketch = newSketch(context, id + "F22", { "sketchPlane" : qUnion([Q0])});
            skLineSegment(sketch, "E77", {"start": v(-2379.92, 150) * mm, "end": v(-2000, 150) * mm});
            skPoint(sketch, "E77.startSnap0", {"position": v(-2115, 150) * mm});
            skLineSegment(sketch, "E78", {"start": v(-2000, 150) * mm, "end": v(-2000, 900) * mm});
            skLineSegment(sketch, "E79", {"start": v(-2000, 900) * mm, "end": v(-2379.92, 900) * mm});
            skLineSegment(sketch, "E80.0", {"start": v(-2015, 885) * mm, "end": v(-2379.92, 885) * mm});
            skLineSegment(sketch, "E80.1", {"start": v(-2015, 165) * mm, "end": v(-2015, 885) * mm});
            skLineSegment(sketch, "E80.2", {"start": v(-2379.92, 165) * mm, "end": v(-2015, 165) * mm});
            skLineSegment(sketch, "E81", {"start": v(-2379.92, 885) * mm, "end": v(-2379.92, 900) * mm});
            skLineSegment(sketch, "E82", {"start": v(-2379.92, 165) * mm, "end": v(-2379.92, 150) * mm});
            skSolve(sketch);
        }
        {
            var Q0;
            {var subQ0=sQuery(id+"F22.wireOp",EDGE,"E78");Q0=makeQuery(id+"F22.imprint","IMPRINT",FACE,{"disambiguationData":[TD([[makeQuery(id+"F22.imprint","IMPRINT",EDGE,{"derivedFrom":subQ0}),-1.0]])]});}
            var Q1;
            {var subQ0=sQuery(id+"F22.wireOp",EDGE,"E81");Q1=makeQuery(id+"F22.imprint","IMPRINT",FACE,{"disambiguationData":[TD([[makeQuery(id+"F22.imprint","IMPRINT",EDGE,{"derivedFrom":subQ0}),-1.0]])]});}
            var Q2;
            {var subQ9=sQuery(id+"F22.wireOp",EDGE,"E82");Q2=makeQuery(id+"F22.imprint","IMPRINT",FACE,{"disambiguationData":[TD([[makeQuery(id+"F22.imprint","IMPRINT",EDGE,{"derivedFrom":subQ9}),1.0]])]});}
            extrude(context, id + "F23", {"entities" : qUnion([Q0, Q1, Q2]), "operationType" : NewBodyOperationType.ADD, "depth" : 835 * mm});
        }
        {
            var Q0;
            Q0=makeQuery(id+"F23.boolean.opBoolean","MERGE",FACE,{"derivedFrom":[makeQuery(id+"F21.opExtrude","CAP_FACE",FACE,{"disambiguationData":[OSD([sQuery(id+"F20.wireOp",EDGE,"E69"),sQuery(id+"F20.wireOp",EDGE,"E70"),sQuery(id+"F20.wireOp",EDGE,"E71"),sQuery(id+"F20.wireOp",EDGE,"E72"),sQuery(id+"F20.wireOp",EDGE,"E73"),sQuery(id+"F20.wireOp",EDGE,"E74"),sQuery(id+"F20.wireOp",EDGE,"E75"),sQuery(id+"F20.wireOp",EDGE,"E76")])],"isStart":false}),makeQuery(id+"F23.opExtrude","CAP_FACE",FACE,{"disambiguationData":[OSD([sQuery(id+"F22.wireOp",EDGE,"E77"),sQuery(id+"F22.wireOp",EDGE,"E78"),sQuery(id+"F22.wireOp",EDGE,"E79"),sQuery(id+"F22.wireOp",EDGE,"E80.0"),sQuery(id+"F22.wireOp",EDGE,"E80.1"),sQuery(id+"F22.wireOp",EDGE,"E80.2"),sQuery(id+"F22.wireOp",EDGE,"E81"),sQuery(id+"F22.wireOp",EDGE,"E82")])],"isStart":false})]});
            var sketch = newSketch(context, id + "F24", { "sketchPlane" : qUnion([Q0])});
            skLineSegment(sketch, "E83", {"start": v(-1650, 150) * mm, "end": v(-2379.92, 150) * mm});
            skLineSegment(sketch, "E84", {"start": v(-2379.92, 150) * mm, "end": v(-2379.92, 900) * mm});
            skLineSegment(sketch, "E85", {"start": v(-2379.92, 900) * mm, "end": v(-1650, 900) * mm});
            skLineSegment(sketch, "E86", {"start": v(-1650, 900) * mm, "end": v(-1650, 885) * mm});
            skLineSegment(sketch, "E87", {"start": v(-1650, 885) * mm, "end": v(-2364.92, 885) * mm});
            skLineSegment(sketch, "E88", {"start": v(-2364.92, 885) * mm, "end": v(-2364.92, 165) * mm});
            skLineSegment(sketch, "E89", {"start": v(-2364.92, 165) * mm, "end": v(-1650, 165) * mm});
            skLineSegment(sketch, "E90", {"start": v(-1650, 165) * mm, "end": v(-1650, 150) * mm});
            skSolve(sketch);
        }
        {
            var Q0;
            {var subQ5=sQuery(id+"F24.wireOp",EDGE,"E88");Q0=makeQuery(id+"F24.imprint","IMPRINT",FACE,{"disambiguationData":[TD([[makeQuery(id+"F24.imprint","IMPRINT",EDGE,{"derivedFrom":subQ5}),-1.0]])]});}
            var Q1;
            {var subQ10=sQuery(id+"F24.wireOp",EDGE,"E90");Q1=makeQuery(id+"F24.imprint","IMPRINT",FACE,{"disambiguationData":[TD([[makeQuery(id+"F24.imprint","IMPRINT",EDGE,{"derivedFrom":subQ10}),1.0]])]});}
            var Q2;
            {var subQ3=sQuery(id+"F24.wireOp",EDGE,"E85");Q2=makeQuery(id+"F24.imprint","IMPRINT",FACE,{"disambiguationData":[TD([[makeQuery(id+"F24.imprint","IMPRINT",EDGE,{"derivedFrom":subQ3}),1.0]])]});}
            extrude(context, id + "F25", {"entities" : qUnion([Q0, Q1, Q2]), "operationType" : NewBodyOperationType.ADD, "depth" : 670 * mm});
        }
        {
            var Q0;
            Q0=makeQuery(id+"F25.opExtrude","SWEPT_FACE",FACE,{"disambiguationData":[OSD([sQuery(id+"F24.wireOp",EDGE,"E88")])]});
            var sketch = newSketch(context, id + "F26", { "sketchPlane" : qUnion([Q0])});
            skLineSegment(sketch, "E91.bottom", {"start": v(100, 165) * mm, "end": v(115, 165) * mm});
            skLineSegment(sketch, "E91.top", {"start": v(100, 885) * mm, "end": v(115, 885) * mm});
            skLineSegment(sketch, "E91.left", {"start": v(100, 165) * mm, "end": v(100, 885) * mm});
            skLineSegment(sketch, "E91.right", {"start": v(115, 165) * mm, "end": v(115, 885) * mm});
            skLineSegment(sketch, "E92.bottom", {"start": v(770, 165) * mm, "end": v(755, 165) * mm});
            skLineSegment(sketch, "E92.top", {"start": v(770, 885) * mm, "end": v(755, 885) * mm});
            skLineSegment(sketch, "E92.left", {"start": v(770, 165) * mm, "end": v(770, 885) * mm});
            skLineSegment(sketch, "E92.right", {"start": v(755, 165) * mm, "end": v(755, 885) * mm});
            skLineSegment(sketch, "E93", {"start": v(515, 165) * mm, "end": v(515, 885) * mm});
            skLineSegment(sketch, "E94.0", {"start": v(530, 165) * mm, "end": v(530, 885) * mm});
            skLineSegment(sketch, "E95", {"start": v(115, 295) * mm, "end": v(515, 295) * mm});
            skLineSegment(sketch, "E96.0", {"start": v(115, 345) * mm, "end": v(515, 345) * mm});
            skLineSegment(sketch, "E97", {"start": v(115, 475) * mm, "end": v(515, 475) * mm});
            skLineSegment(sketch, "E98.0", {"start": v(115, 525) * mm, "end": v(515, 525) * mm});
            skLineSegment(sketch, "E99", {"start": v(115, 655) * mm, "end": v(515, 655) * mm});
            skLineSegment(sketch, "E100.0", {"start": v(115, 705) * mm, "end": v(515, 705) * mm});
            skLineSegment(sketch, "E101", {"start": v(115, 835) * mm, "end": v(515, 835) * mm});
            skLineSegment(sketch, "E102", {"start": v(115, 885) * mm, "end": v(515, 885) * mm});
            skLineSegment(sketch, "E103", {"start": v(115, 885) * mm, "end": v(115, 835) * mm});
            skLineSegment(sketch, "E104", {"start": v(515, 885) * mm, "end": v(515, 835) * mm});
            skLineSegment(sketch, "E105", {"start": v(515, 705) * mm, "end": v(515, 655) * mm});
            skLineSegment(sketch, "E106", {"start": v(115, 705) * mm, "end": v(115, 655) * mm});
            skLineSegment(sketch, "E107", {"start": v(115, 525) * mm, "end": v(115, 475) * mm});
            skLineSegment(sketch, "E108", {"start": v(515, 525) * mm, "end": v(515, 475) * mm});
            skLineSegment(sketch, "E109", {"start": v(115, 345) * mm, "end": v(115, 295) * mm});
            skLineSegment(sketch, "E110", {"start": v(515, 295) * mm, "end": v(515, 345) * mm});
            skSolve(sketch);
        }
        {
            var Q0;
            {var subQ2=sQuery(id+"F26.wireOp",EDGE,"E94.0");Q0=makeQuery(id+"F26.imprint","IMPRINT",FACE,{"disambiguationData":[TD([[makeQuery(id+"F26.imprint","IMPRINT",EDGE,{"derivedFrom":subQ2}),1.0]])]});}
            var Q1;
            Q1=makeQuery(id+"F26.imprint","IMPRINT",FACE,{"disambiguationData":[TD([[makeQuery(id+"F26.imprint","IMPRINT",EDGE,{"derivedFrom":sQuery(id+"F26.wireOp",EDGE,"E101")}),1.0]])]});
            var Q2;
            Q2=makeQuery(id+"F26.imprint","IMPRINT",FACE,{"disambiguationData":[TD([[makeQuery(id+"F26.imprint","IMPRINT",EDGE,{"derivedFrom":sQuery(id+"F26.wireOp",EDGE,"E99")}),1.0]])]});
            var Q3;
            Q3=makeQuery(id+"F26.imprint","IMPRINT",FACE,{"disambiguationData":[TD([[makeQuery(id+"F26.imprint","IMPRINT",EDGE,{"derivedFrom":sQuery(id+"F26.wireOp",EDGE,"E97")}),1.0]])]});
            var Q4;
            Q4=makeQuery(id+"F26.imprint","IMPRINT",FACE,{"disambiguationData":[TD([[makeQuery(id+"F26.imprint","IMPRINT",EDGE,{"derivedFrom":sQuery(id+"F26.wireOp",EDGE,"E92.bottom")}),1.0]])]});
            var Q5;
            Q5=makeQuery(id+"F26.imprint","IMPRINT",FACE,{"disambiguationData":[TD([[makeQuery(id+"F26.imprint","IMPRINT",EDGE,{"derivedFrom":sQuery(id+"F26.wireOp",EDGE,"E95")}),1.0]])]});
            var Q6;
            {var subQ4=sQuery(id+"F26.wireOp",EDGE,"E91.bottom");Q6=makeQuery(id+"F26.imprint","IMPRINT",FACE,{"disambiguationData":[TD([[makeQuery(id+"F26.imprint","IMPRINT",EDGE,{"derivedFrom":subQ4}),1.0]])]});}
            extrude(context, id + "F27", {"entities" : qUnion([Q0, Q1, Q2, Q3, Q4, Q5, Q6]), "operationType" : NewBodyOperationType.ADD, "depth" : 715 * mm});
        }
        {
            var Q0;
            Q0=makeQuery(id+"F25.boolean.opBoolean","MERGE",FACE,{"derivedFrom":[makeQuery(id+"F23.boolean.opBoolean","MERGE",FACE,{"derivedFrom":[makeQuery(id+"F21.boolean.opBoolean","MERGE",FACE,{"derivedFrom":[makeQuery(id+"F15.boolean.opBoolean","MERGE",FACE,{"derivedFrom":[makeQuery(id+"F13.opExtrude","SWEPT_FACE",FACE,{"disambiguationData":[OSD([sQuery(id+"F12.wireOp",EDGE,"E47.top")])]}),makeQuery(id+"F15.opExtrude","SWEPT_FACE",FACE,{"disambiguationData":[OSD([sQuery(id+"F14.wireOp",EDGE,"E60")])]})]}),makeQuery(id+"F21.opExtrude","SWEPT_FACE",FACE,{"disambiguationData":[OSD([sQuery(id+"F20.wireOp",EDGE,"E71")])]})]}),makeQuery(id+"F23.opExtrude","SWEPT_FACE",FACE,{"disambiguationData":[OSD([sQuery(id+"F22.wireOp",EDGE,"E79")])]})]}),makeQuery(id+"F25.opExtrude","SWEPT_FACE",FACE,{"disambiguationData":[OSD([sQuery(id+"F24.wireOp",EDGE,"E85")])]})]});
            var sketch = newSketch(context, id + "F28", { "sketchPlane" : qUnion([Q0])});
            skLineSegment(sketch, "E111", {"start": v(-1605, -2000) * mm, "end": v(-1605, -2473.83) * mm});
            skPoint(sketch, "E111.endSnap0", {"position": v(-1605, -2304.96) * mm});
            skLineSegment(sketch, "E112", {"start": v(-1605, -2473.83) * mm, "end": v(0, -2473.83) * mm});
            skLineSegment(sketch, "E113", {"start": v(0, -2473.83) * mm, "end": v(0, -1609.82) * mm});
            skLineSegment(sketch, "E114", {"start": v(0, -1609.82) * mm, "end": v(-1431.39, -1609.82) * mm});
            skLineSegment(sketch, "E115", {"start": v(-1431.39, -1609.82) * mm, "end": v(-1431.39, -766.5) * mm});
            skLineSegment(sketch, "E116", {"start": v(-1431.39, -766.5) * mm, "end": v(-810, -766.5) * mm});
            skLineSegment(sketch, "E117", {"start": v(-810, -766.5) * mm, "end": v(-810, -130) * mm});
            skLineSegment(sketch, "E118", {"start": v(-810, -130) * mm, "end": v(-2070, -130) * mm});
            skLineSegment(sketch, "E119", {"start": v(-2070, -130) * mm, "end": v(-2070, -2000) * mm});
            skLineSegment(sketch, "E120", {"start": v(-2070, -2000) * mm, "end": v(-1605, -2000) * mm});
            skSolve(sketch);
        }
        {
            var Q0;
            {var subQ6=sQuery(id+"F28.wireOp",EDGE,"E118");Q0=makeQuery(id+"F28.imprint","IMPRINT",FACE,{"disambiguationData":[TD([[makeQuery(id+"F28.imprint","IMPRINT",EDGE,{"derivedFrom":subQ6}),1.0]])]});}
            var Q1;
            {var subQ6=sQuery(id+"F28.wireOp",EDGE,"E112");Q1=makeQuery(id+"F28.imprint","IMPRINT",FACE,{"disambiguationData":[TD([[makeQuery(id+"F28.imprint","IMPRINT",EDGE,{"derivedFrom":subQ6}),1.0]])]});}
            extrude(context, id + "F29", {"entities" : qUnion([Q0, Q1]), "operationType" : NewBodyOperationType.ADD, "depth" : 40 * mm});
        }
        {
            var Q0;
            Q0=makeQuery(id+"F23.opExtrude","SWEPT_FACE",FACE,{"disambiguationData":[OSD([sQuery(id+"F22.wireOp",EDGE,"E80.1")])]});
            var sketch = newSketch(context, id + "F30", { "sketchPlane" : qUnion([Q0])});
            skLineSegment(sketch, "E121.bottom", {"start": v(-1605, 517) * mm, "end": v(-770, 517) * mm});
            skLineSegment(sketch, "E121.top", {"start": v(-1605, 532) * mm, "end": v(-770, 532) * mm});
            skLineSegment(sketch, "E121.left", {"start": v(-1605, 532) * mm, "end": v(-1605, 517) * mm});
            skLineSegment(sketch, "E121.right", {"start": v(-770, 532) * mm, "end": v(-770, 517) * mm});
            skSolve(sketch);
        }
        {
            var Q0;
            Q0=makeQuery(id+"F30.imprint","IMPRINT",FACE,{"disambiguationData":[TD([[makeQuery(id+"F30.imprint","IMPRINT",EDGE,{"derivedFrom":sQuery(id+"F30.wireOp",EDGE,"E121.bottom")}),1.0]])]});
            var Q1;
            Q1=makeQuery(id+"F25.boolean.opBoolean","MERGE",FACE,{"derivedFrom":[makeQuery(id+"F23.opExtrude","SWEPT_FACE",FACE,{"disambiguationData":[OSD([sQuery(id+"F22.wireOp",EDGE,"E81")])]}),makeQuery(id+"F23.opExtrude","SWEPT_FACE",FACE,{"disambiguationData":[OSD([sQuery(id+"F22.wireOp",EDGE,"E82")])]}),makeQuery(id+"F25.opExtrude","SWEPT_FACE",FACE,{"disambiguationData":[OSD([sQuery(id+"F24.wireOp",EDGE,"E84")])]})]});
            extrude(context, id + "F31", {"entities" : qUnion([Q0]), "operationType" : NewBodyOperationType.ADD, "endBound" : BoundingType.UP_TO_SURFACE, "endBoundEntityFace" : qUnion([Q1]), "depth" : 25 * mm});
        }
    });
